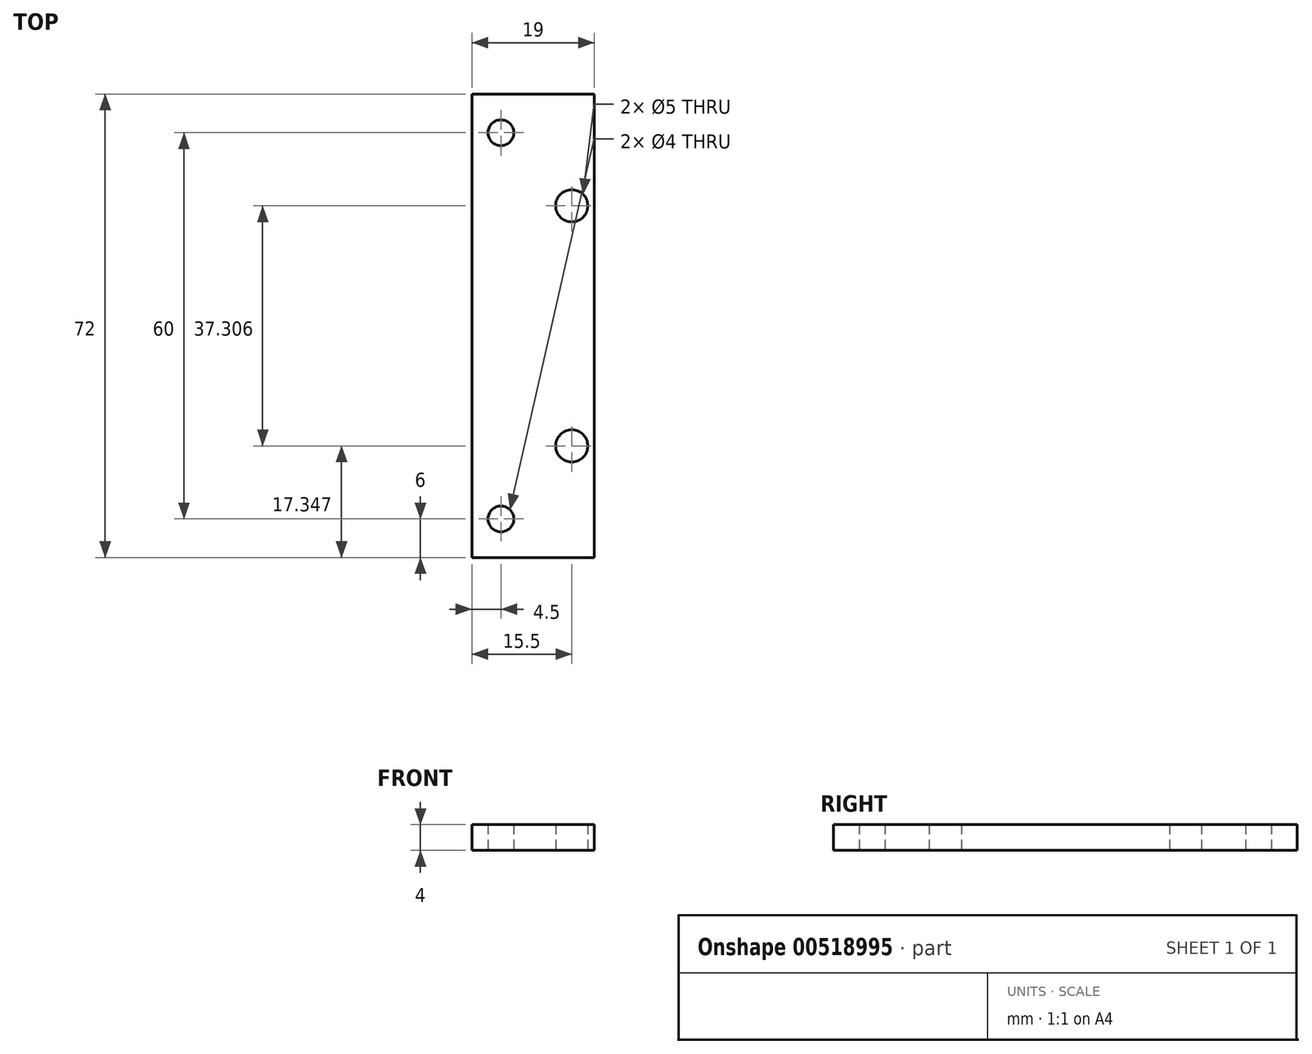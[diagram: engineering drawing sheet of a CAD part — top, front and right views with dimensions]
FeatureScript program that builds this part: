
annotation { "Feature Type Name" : "Feature", "Feature Type Description" : "" }
export const myFeature = defineFeature(function(context is Context, id is Id, definition is map)
    precondition{}
    {
        {
            var Q0;
            Q0=qCreatedBy(makeId("Top.planeOp"),FACE);
            var sketch = newSketch(context, id + "F0", { "sketchPlane" : qUnion([Q0])});
            skLineSegment(sketch, "E0.bottom", {"start": v(9.5, -36) * mm, "end": v(-9.5, -36) * mm});
            skLineSegment(sketch, "E0.top", {"start": v(9.5, 36) * mm, "end": v(-9.5, 36) * mm});
            skLineSegment(sketch, "E0.left", {"start": v(9.5, -36) * mm, "end": v(9.5, 36) * mm});
            skLineSegment(sketch, "E0.right", {"start": v(-9.5, -36) * mm, "end": v(-9.5, 36) * mm});
            skPoint(sketch, "E0.middle", {"position": v(0, 0) * mm});
            skCircle(sketch, "E1", {"center": v(6, 18.65) * mm, "radius": 2.5 * mm});
            skCircle(sketch, "E2", {"center": v(6, -18.65) * mm, "radius": 2.5 * mm});
            skLineSegment(sketch, "E3", {"start": v(6, 18.65) * mm, "end": v(6, 36) * mm, "construction": true});
            skLineSegment(sketch, "E4", {"start": v(6, -18.65) * mm, "end": v(6, -36) * mm, "construction": true});
            skCircle(sketch, "E5", {"center": v(-5, 30) * mm, "radius": 2 * mm});
            skCircle(sketch, "E6", {"center": v(-5, -30) * mm, "radius": 2 * mm});
            skLineSegment(sketch, "E7", {"start": v(-5, -30) * mm, "end": v(-9.5, -30) * mm, "construction": true});
            skLineSegment(sketch, "E8", {"start": v(-5, -30) * mm, "end": v(-5, -36) * mm, "construction": true});
            skLineSegment(sketch, "E9", {"start": v(-5, 30) * mm, "end": v(-5, 36) * mm, "construction": true});
            skSolve(sketch);
        }
        {
            var Q0;
            Q0=makeQuery(id+"F0.imprint","IMPRINT",FACE,{"disambiguationData":[TD([[makeQuery(id+"F0.imprint","IMPRINT",EDGE,{"derivedFrom":sQuery(id+"F0.wireOp",EDGE,"E0.bottom")}),-1.0]])]});
            extrude(context, id + "F1", {"entities" : qUnion([Q0]), "depth" : 4 * mm, "offsetDistance" : 25 * mm});
        }
    });
